# Revit family: EKF_EE_КомплектПанелейЦоколяFORT_PROxima
name_source: partatom
category: Электрооборудование
units: mm (PartAtom-declared; Revit-internal decimal feet)

## family parameters
Всегда вертикально = Нет
На основе рабочей плоскости = Да
Общий = Да
При загрузке вырезать с полостями = Нет
Размер круглого соединителя = Использовать диаметр
Тип детали = Силовой щит
Точка расчета площади = Нет

## types (4) — shared parameters
ADSK_Единица измерения = шт.
ADSK_Завод-изготовитель = EKF
ADSK_Количество = 1
ADSK_Марка = Комплект панелей цоколя FORT
ADSK_Материал = RAL 7035_Сталь
ADSK_Обозначение = Комплект панелей цоколя FORT
ADSK_Размер_Высота = 200 мм
ADSK_Размер_Глубина = 12.5 мм
t = 1 мм
Изготовитель = EKF
Отв_Отступ = 20 мм
Серия номенклатуры = PROxima
Степень защиты IP = -
ТВ = EKF_2
Тип установки = -
zero-valued in all types: ADSK_Масса, Отметка по умолчанию

## per-type parameters (varying)
| type | ADSK_Код изделия | ADSK_Наименование | ADSK_Размер_Ширина | Тип |
| Комплект панелей цоколя FORT Ш1000 В200 PROxima (2шт) | FC102 | Комплект панелей цоколя FORT Ш1000 В200 PROxima (2шт) | 1000 мм | 269 мм |
| Комплект панелей цоколя FORT Ш400 В200  PROxima (2шт) | FC42 | Комплект панелей цоколя FORT Ш400 В200 PROxima (2шт) | 400 мм | 270 мм |
| Комплект панелей цоколя FORT Ш600 В200 PROxima (2шт) | FC62 | Комплект панелей цоколя FORT Ш600 В200 PROxima (2шт) | 600 мм | 271 мм |
| Комплект панелей цоколя FORT Ш800 В200 PROxima (2 шт) | FC82 | Комплект панелей цоколя FORT Ш800 В200 PROxima (2 шт) | 800 мм | 272 мм |
